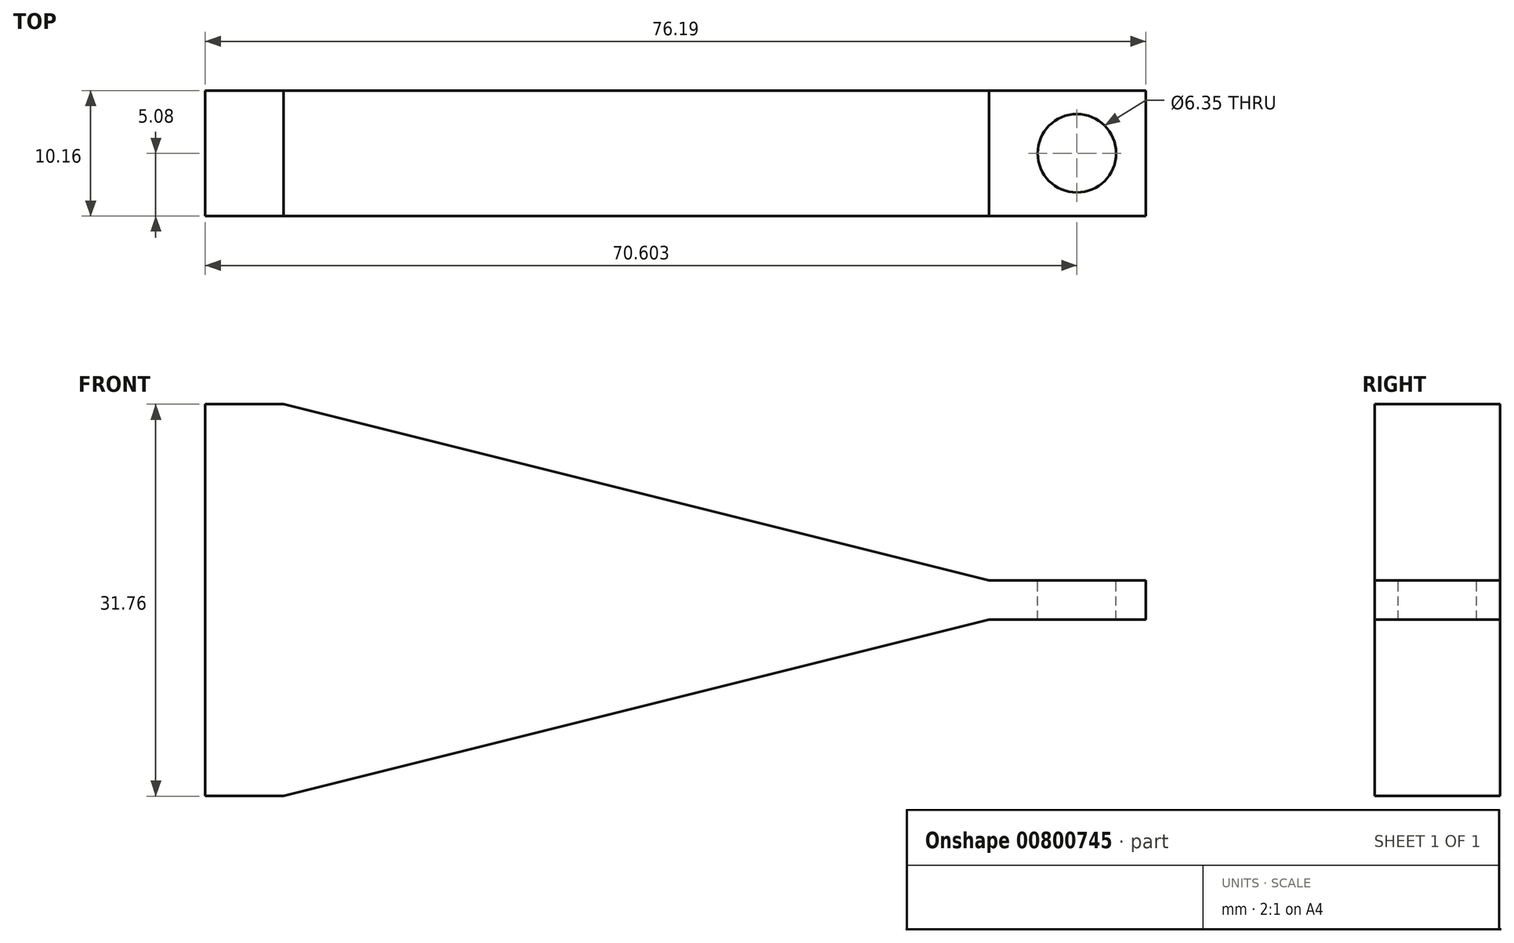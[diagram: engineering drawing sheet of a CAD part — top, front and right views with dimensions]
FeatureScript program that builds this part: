
annotation { "Feature Type Name" : "Feature", "Feature Type Description" : "" }
export const myFeature = defineFeature(function(context is Context, id is Id, definition is map)
    precondition{}
    {
        {
            var Q0;
            Q0=qCreatedBy(makeId("Front.planeOp"),FACE);
            var sketch = newSketch(context, id + "F0", { "sketchPlane" : qUnion([Q0])});
            skLineSegment(sketch, "E0.bottom", {"start": v(34.93, -15.88) * mm, "end": v(-34.93, -15.88) * mm});
            skLineSegment(sketch, "E0.top", {"start": v(34.93, 15.87) * mm, "end": v(-34.93, 15.87) * mm});
            skLineSegment(sketch, "E0.left", {"start": v(34.93, -15.88) * mm, "end": v(34.93, 15.87) * mm});
            skLineSegment(sketch, "E0.right", {"start": v(-34.93, -15.88) * mm, "end": v(-34.93, 15.87) * mm});
            skPoint(sketch, "E0.middle", {"position": v(0, 0) * mm});
            skLineSegment(sketch, "E1.bottom", {"start": v(-34.93, 15.87) * mm, "end": v(-28.58, 15.87) * mm, "construction": true});
            skLineSegment(sketch, "E1.top", {"start": v(-34.93, -15.88) * mm, "end": v(-28.57, -15.88) * mm, "construction": true});
            skLineSegment(sketch, "E1.left", {"start": v(-34.93, 15.87) * mm, "end": v(-34.93, -15.88) * mm, "construction": true});
            skLineSegment(sketch, "E1.right", {"start": v(-28.58, 15.87) * mm, "end": v(-28.57, -15.88) * mm, "construction": true});
            skLineSegment(sketch, "E2", {"start": v(-28.57, 15.87) * mm, "end": v(34.92, 0) * mm});
            skLineSegment(sketch, "E3", {"start": v(34.92, 0) * mm, "end": v(-28.57, -15.88) * mm});
            skLineSegment(sketch, "E4.bottom", {"start": v(34.93, 15.87) * mm, "end": v(28.57, 15.87) * mm});
            skLineSegment(sketch, "E4.top", {"start": v(34.93, -15.88) * mm, "end": v(28.58, -15.88) * mm});
            skLineSegment(sketch, "E4.left", {"start": v(34.93, 15.87) * mm, "end": v(34.93, -15.88) * mm});
            skLineSegment(sketch, "E4.right", {"start": v(28.57, 15.88) * mm, "end": v(28.58, -15.88) * mm});
            skSolve(sketch);
        }
        {
            var Q0;
            {var subQ5=sQuery(id+"F0.wireOp",EDGE,"E0.right");Q0=makeQuery(id+"F0.imprint","IMPRINT",FACE,{"disambiguationData":[TD([[makeQuery(id+"F0.imprint","IMPRINT",EDGE,{"derivedFrom":subQ5}),-1.0]])]});}
            extrude(context, id + "F1", {"entities" : qUnion([Q0]), "endBound" : BoundingType.SYMMETRIC, "depth" : 10.16 * mm, "offsetDistance" : 25.4 * mm});
        }
        {
            var Q0;
            Q0=makeQuery(id+"F1.opExtrude","SWEPT_FACE",FACE,{"disambiguationData":[OSD([sQuery(id+"F0.wireOp",EDGE,"E4.right")])]});
            var sketch = newSketch(context, id + "F2", { "sketchPlane" : qUnion([Q0])});
            skLineSegment(sketch, "E5.bottom", {"start": v(-5.08, 1.59) * mm, "end": v(5.08, 1.59) * mm});
            skLineSegment(sketch, "E5.top", {"start": v(-5.08, -1.59) * mm, "end": v(5.08, -1.59) * mm});
            skLineSegment(sketch, "E5.left", {"start": v(-5.08, 1.59) * mm, "end": v(-5.08, -1.59) * mm});
            skLineSegment(sketch, "E5.right", {"start": v(5.08, 1.59) * mm, "end": v(5.08, -1.59) * mm});
            skSolve(sketch);
        }
        {
            var Q0;
            Q0=makeQuery(id+"F2.imprint","IMPRINT",FACE,{"disambiguationData":[TD([[makeQuery(id+"F2.imprint","IMPRINT",EDGE,{"derivedFrom":sQuery(id+"F2.wireOp",EDGE,"E5.bottom")}),-1.0]])]});
            extrude(context, id + "F3", {"entities" : qUnion([Q0]), "operationType" : NewBodyOperationType.ADD, "depth" : 12.7 * mm, "offsetDistance" : 25.4 * mm});
        }
        {
            var Q0;
            Q0=makeQuery(id+"F3.opExtrude","SWEPT_FACE",FACE,{"disambiguationData":[OSD([sQuery(id+"F2.wireOp",EDGE,"E5.bottom")])]});
            var sketch = newSketch(context, id + "F4", { "sketchPlane" : qUnion([Q0])});
            skCircle(sketch, "E6", {"center": v(35.68, 0) * mm, "radius": 3.18 * mm});
            skSolve(sketch);
        }
        {
            var Q0;
            Q0=makeQuery(id+"F4.imprint","IMPRINT",FACE,{"disambiguationData":[TD([[makeQuery(id+"F4.imprint","IMPRINT",EDGE,{"derivedFrom":sQuery(id+"F4.wireOp",EDGE,"E6")}),1.0]])]});
            extrude(context, id + "F5", {"entities" : qUnion([Q0]), "operationType" : NewBodyOperationType.REMOVE, "oppositeDirection" : true, "depth" : 25.4 * mm, "offsetDistance" : 25.4 * mm});
        }
    });
